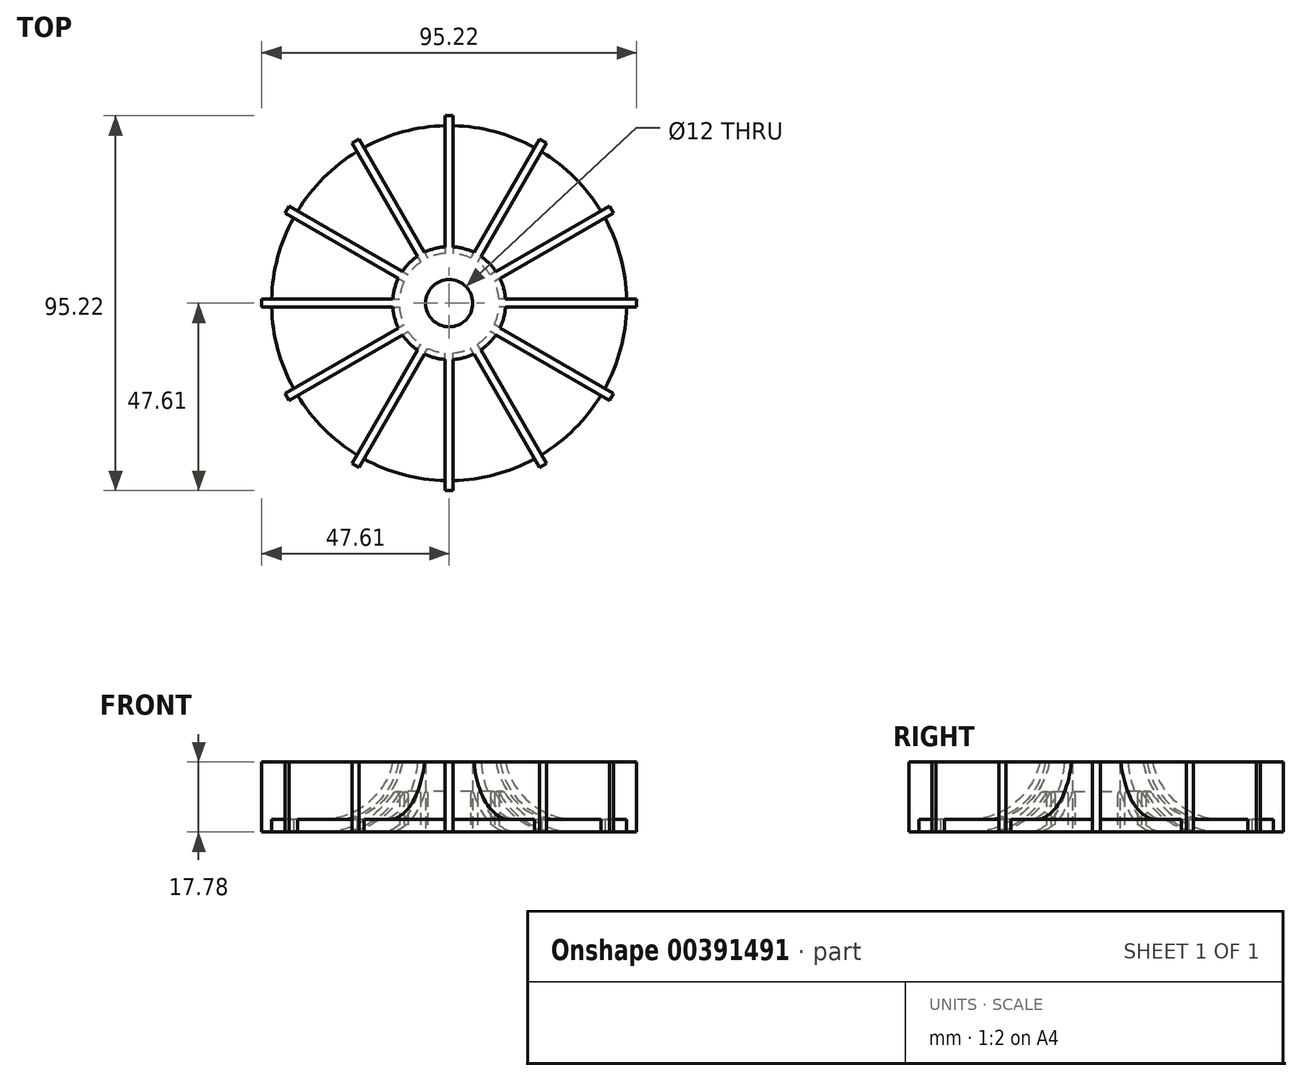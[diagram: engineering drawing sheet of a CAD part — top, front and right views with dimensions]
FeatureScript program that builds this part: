
annotation { "Feature Type Name" : "Feature", "Feature Type Description" : "" }
export const myFeature = defineFeature(function(context is Context, id is Id, definition is map)
    precondition{}
    {
        {
            var Q0;
            Q0=qCreatedBy(makeId("Front.planeOp"),FACE);
            var sketch = newSketch(context, id + "F0", { "sketchPlane" : qUnion([Q0])});
            skLineSegment(sketch, "E0", {"start": v(-12.7, 0) * mm, "end": v(-12.7, 12.7) * mm, "construction": true});
            skPoint(sketch, "E1", {"position": v(-45.09, 0) * mm});
            skPoint(sketch, "E2", {"position": v(-32.38, 0) * mm});
            skLineSegment(sketch, "E3", {"start": v(-45.09, 0) * mm, "end": v(-32.38, 0) * mm});
            skArc(sketch, "E4", {"start": v(-32.38, 0) * mm, "mid": v(-22.04, 2.64) * mm, "end": v(-14.22, 9.9) * mm});
            skLineSegment(sketch, "E5", {"start": v(-12.7, 9.46) * mm, "end": v(-12.7, 0) * mm});
            skPoint(sketch, "E6.visualSharp", {"position": v(-12.7, 12.7) * mm});
            skArc(sketch, "E6.filletArc", {"start": v(-12.7, 9.46) * mm, "mid": v(-13.3, 10.25) * mm, "end": v(-14.22, 9.9) * mm});
            skLineSegment(sketch, "E7", {"start": v(-12.7, 0) * mm, "end": v(0, 0) * mm});
            skLineSegment(sketch, "E8", {"start": v(0, 0) * mm, "end": v(0, 17.78) * mm});
            skArc(sketch, "E9.0", {"start": v(-32.38, 3.18) * mm, "mid": v(-20.78, 7.28) * mm, "end": v(-14.36, 17.78) * mm});
            skLineSegment(sketch, "E9.1", {"start": v(-45.09, 3.18) * mm, "end": v(-32.38, 3.18) * mm});
            skLineSegment(sketch, "E10", {"start": v(-45.09, 3.18) * mm, "end": v(-45.09, 0) * mm});
            skLineSegment(sketch, "E11", {"start": v(0, 17.78) * mm, "end": v(-14.36, 17.78) * mm});
            skSolve(sketch);
        }
        {
            var Q0;
            Q0=makeQuery(id+"F0.imprint","IMPRINT",FACE,{"disambiguationData":[TD([[makeQuery(id+"F0.imprint","IMPRINT",EDGE,{"derivedFrom":sQuery(id+"F0.wireOp",EDGE,"E3")}),1.0]])]});
            var Q1;
            Q1=sQuery(id+"F0.wireOp",EDGE,"E8");
            revolve(context, id + "F1", {"entities" : qUnion([Q0]), "axis" : qUnion([Q1]), "revolveType" : RevolveType.FULL});
        }
        {
            var Q0;
            Q0=makeQuery(id+"F1.opRevolve","SWEPT_FACE",FACE,{"disambiguationData":[OSD([sQuery(id+"F0.wireOp",EDGE,"E7")])]});
            var sketch = newSketch(context, id + "F2", { "sketchPlane" : qUnion([Q0])});
            skCircle(sketch, "E12", {"center": v(0, 0) * mm, "radius": 6 * mm});
            skSolve(sketch);
        }
        {
            var Q0;
            Q0=makeQuery(id+"F2.imprint","IMPRINT",FACE,{"disambiguationData":[TD([[makeQuery(id+"F2.imprint","IMPRINT",EDGE,{"derivedFrom":sQuery(id+"F2.wireOp",EDGE,"E12")}),1.0]])]});
            extrude(context, id + "F3", {"entities" : qUnion([Q0]), "operationType" : NewBodyOperationType.REMOVE, "oppositeDirection" : true, "offsetDistance" : 25.4 * mm, "depth" : 25.4 * mm});
        }
        {
            var Q0;
            Q0=makeQuery(id+"F1.opRevolve","SWEPT_FACE",FACE,{"disambiguationData":[OSD([sQuery(id+"F0.wireOp",EDGE,"E9.1")])]});
            var sketch = newSketch(context, id + "F4", { "sketchPlane" : qUnion([Q0])});
            skLineSegment(sketch, "E13", {"start": v(0, 0) * mm, "end": v(-45.09, 0) * mm, "construction": true});
            skLineSegment(sketch, "E14.bottom", {"start": v(-47.61, -1.02) * mm, "end": v(-9.51, -1.02) * mm});
            skLineSegment(sketch, "E14.top", {"start": v(-47.61, 1.02) * mm, "end": v(-9.51, 1.02) * mm});
            skLineSegment(sketch, "E14.left", {"start": v(-47.61, -1.02) * mm, "end": v(-47.61, 1.02) * mm});
            skLineSegment(sketch, "E14.right", {"start": v(-9.51, -1.02) * mm, "end": v(-9.51, 1.02) * mm});
            skPoint(sketch, "E14.middle", {"position": v(-28.56, 0) * mm});
            skLineSegment(sketch, "E15.1.0", {"start": v(-7.73, -5.64) * mm, "end": v(-8.75, -3.88) * mm});
            skLineSegment(sketch, "E15.1.1", {"start": v(-41.74, -22.93) * mm, "end": v(-8.75, -3.88) * mm});
            skLineSegment(sketch, "E15.1.2", {"start": v(-40.73, -24.69) * mm, "end": v(-7.73, -5.64) * mm});
            skLineSegment(sketch, "E15.1.3", {"start": v(-40.73, -24.69) * mm, "end": v(-41.74, -22.93) * mm});
            skLineSegment(sketch, "E15.2.0", {"start": v(-3.88, -8.75) * mm, "end": v(-5.64, -7.73) * mm});
            skLineSegment(sketch, "E15.2.1", {"start": v(-24.69, -40.73) * mm, "end": v(-5.64, -7.73) * mm});
            skLineSegment(sketch, "E15.2.2", {"start": v(-22.93, -41.74) * mm, "end": v(-3.88, -8.75) * mm});
            skLineSegment(sketch, "E15.2.3", {"start": v(-22.93, -41.74) * mm, "end": v(-24.69, -40.73) * mm});
            skLineSegment(sketch, "E15.3.0", {"start": v(1.02, -9.51) * mm, "end": v(-1.02, -9.51) * mm});
            skLineSegment(sketch, "E15.3.1", {"start": v(-1.02, -47.61) * mm, "end": v(-1.02, -9.51) * mm});
            skLineSegment(sketch, "E15.3.2", {"start": v(1.02, -47.61) * mm, "end": v(1.02, -9.51) * mm});
            skLineSegment(sketch, "E15.3.3", {"start": v(1.02, -47.61) * mm, "end": v(-1.02, -47.61) * mm});
            skLineSegment(sketch, "E15.4.0", {"start": v(5.64, -7.73) * mm, "end": v(3.88, -8.75) * mm});
            skLineSegment(sketch, "E15.4.1", {"start": v(22.93, -41.74) * mm, "end": v(3.88, -8.75) * mm});
            skLineSegment(sketch, "E15.4.2", {"start": v(24.69, -40.73) * mm, "end": v(5.64, -7.73) * mm});
            skLineSegment(sketch, "E15.4.3", {"start": v(24.69, -40.73) * mm, "end": v(22.93, -41.74) * mm});
            skLineSegment(sketch, "E15.5.0", {"start": v(8.75, -3.88) * mm, "end": v(7.73, -5.64) * mm});
            skLineSegment(sketch, "E15.5.1", {"start": v(40.73, -24.69) * mm, "end": v(7.73, -5.64) * mm});
            skLineSegment(sketch, "E15.5.2", {"start": v(41.74, -22.93) * mm, "end": v(8.75, -3.88) * mm});
            skLineSegment(sketch, "E15.5.3", {"start": v(41.74, -22.93) * mm, "end": v(40.73, -24.69) * mm});
            skLineSegment(sketch, "E15.6.0", {"start": v(9.51, 1.02) * mm, "end": v(9.51, -1.02) * mm});
            skLineSegment(sketch, "E15.6.1", {"start": v(47.61, -1.02) * mm, "end": v(9.51, -1.02) * mm});
            skLineSegment(sketch, "E15.6.2", {"start": v(47.61, 1.02) * mm, "end": v(9.51, 1.02) * mm});
            skLineSegment(sketch, "E15.6.3", {"start": v(47.61, 1.02) * mm, "end": v(47.61, -1.02) * mm});
            skLineSegment(sketch, "E15.7.0", {"start": v(7.73, 5.64) * mm, "end": v(8.75, 3.88) * mm});
            skLineSegment(sketch, "E15.7.1", {"start": v(41.74, 22.93) * mm, "end": v(8.75, 3.88) * mm});
            skLineSegment(sketch, "E15.7.2", {"start": v(40.73, 24.69) * mm, "end": v(7.73, 5.64) * mm});
            skLineSegment(sketch, "E15.7.3", {"start": v(40.73, 24.69) * mm, "end": v(41.74, 22.93) * mm});
            skLineSegment(sketch, "E15.8.0", {"start": v(3.88, 8.75) * mm, "end": v(5.64, 7.73) * mm});
            skLineSegment(sketch, "E15.8.1", {"start": v(24.69, 40.73) * mm, "end": v(5.64, 7.73) * mm});
            skLineSegment(sketch, "E15.8.2", {"start": v(22.93, 41.74) * mm, "end": v(3.88, 8.75) * mm});
            skLineSegment(sketch, "E15.8.3", {"start": v(22.93, 41.74) * mm, "end": v(24.69, 40.73) * mm});
            skLineSegment(sketch, "E15.9.0", {"start": v(-1.02, 9.51) * mm, "end": v(1.02, 9.51) * mm});
            skLineSegment(sketch, "E15.9.1", {"start": v(1.02, 47.61) * mm, "end": v(1.02, 9.51) * mm});
            skLineSegment(sketch, "E15.9.2", {"start": v(-1.02, 47.61) * mm, "end": v(-1.02, 9.51) * mm});
            skLineSegment(sketch, "E15.9.3", {"start": v(-1.02, 47.61) * mm, "end": v(1.02, 47.61) * mm});
            skLineSegment(sketch, "E15.10.0", {"start": v(-5.64, 7.73) * mm, "end": v(-3.88, 8.75) * mm});
            skLineSegment(sketch, "E15.10.1", {"start": v(-22.93, 41.74) * mm, "end": v(-3.88, 8.75) * mm});
            skLineSegment(sketch, "E15.10.2", {"start": v(-24.69, 40.73) * mm, "end": v(-5.64, 7.73) * mm});
            skLineSegment(sketch, "E15.10.3", {"start": v(-24.69, 40.73) * mm, "end": v(-22.93, 41.74) * mm});
            skLineSegment(sketch, "E15.11.0", {"start": v(-8.75, 3.88) * mm, "end": v(-7.73, 5.64) * mm});
            skLineSegment(sketch, "E15.11.1", {"start": v(-40.73, 24.69) * mm, "end": v(-7.73, 5.64) * mm});
            skLineSegment(sketch, "E15.11.2", {"start": v(-41.74, 22.93) * mm, "end": v(-8.75, 3.88) * mm});
            skLineSegment(sketch, "E15.11.3", {"start": v(-41.74, 22.93) * mm, "end": v(-40.73, 24.69) * mm});
            skPoint(sketch, "E15.center", {"position": v(0, 0) * mm});
            skSolve(sketch);
        }
        {
            var Q0;
            Q0 = qSketchRegion(id + "F4", true);
            var Q1;
            Q1=makeQuery(id+"F1.opRevolve","SWEPT_FACE",FACE,{"disambiguationData":[OSD([sQuery(id+"F0.wireOp",EDGE,"E11")])]});
            var Q2;
            Q2=makeQuery(id+"F1.opRevolve","SWEPT_FACE",FACE,{"disambiguationData":[OSD([sQuery(id+"F0.wireOp",EDGE,"E3")])]});
            extrude(context, id + "F5", {"entities" : qUnion([Q0]), "operationType" : NewBodyOperationType.ADD, "endBound" : BoundingType.UP_TO_SURFACE, "depth" : 25.4 * mm, "endBoundEntityFace" : qUnion([Q1]), "offsetDistance" : 25.4 * mm, "hasSecondDirection" : true, "secondDirectionBound" : BoundingType.UP_TO_SURFACE, "secondDirectionOppositeDirection" : true, "secondDirectionDepth" : 25.4 * mm, "secondDirectionBoundEntityFace" : qUnion([Q2])});
        }
    });
